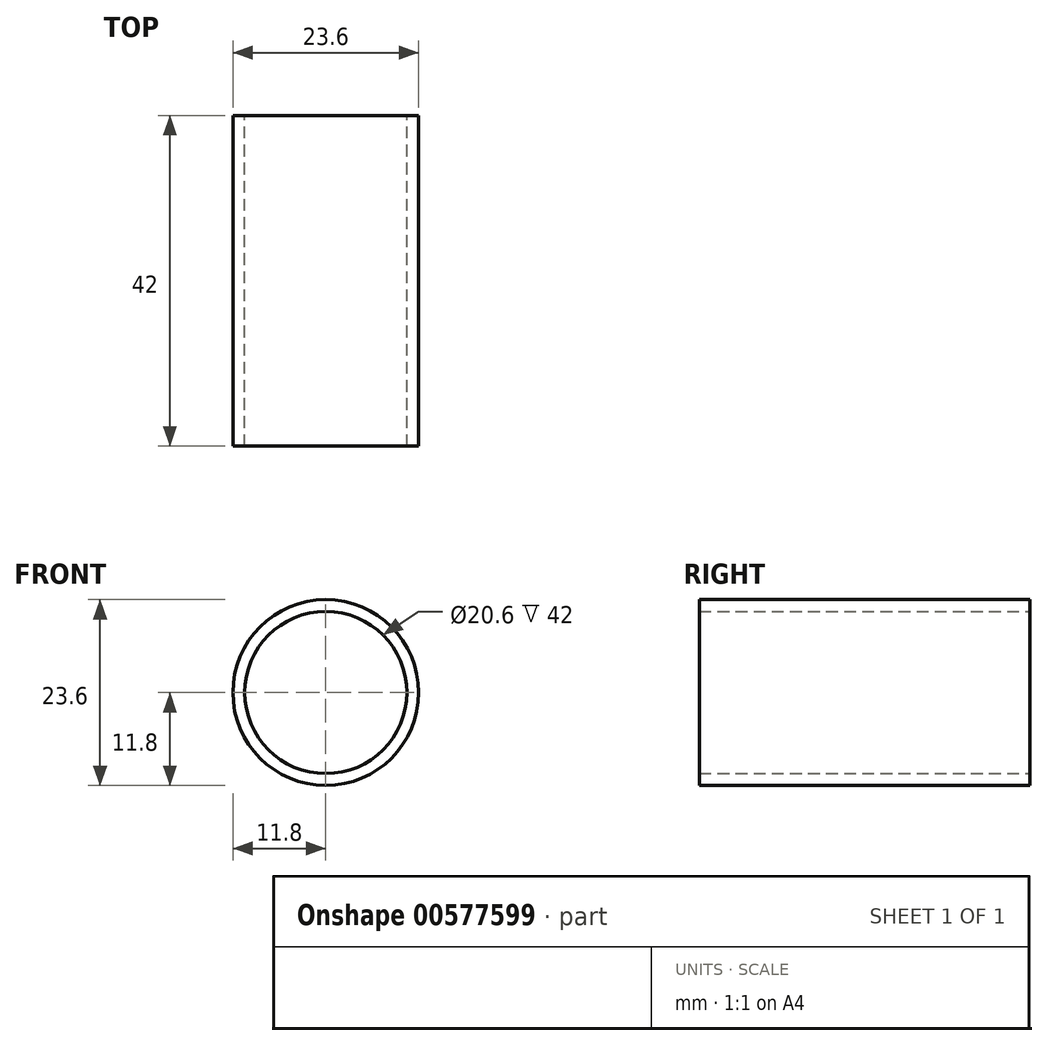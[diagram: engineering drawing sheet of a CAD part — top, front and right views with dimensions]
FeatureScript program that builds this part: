
annotation { "Feature Type Name" : "Feature", "Feature Type Description" : "" }
export const myFeature = defineFeature(function(context is Context, id is Id, definition is map)
    precondition{}
    {
        {
            var Q0;
            Q0=qCreatedBy(makeId("Front.planeOp"),FACE);
            var sketch = newSketch(context, id + "F0", { "sketchPlane" : qUnion([Q0])});
            skCircle(sketch, "E0", {"center": v(0, 0) * mm, "radius": 11.8 * mm});
            skCircle(sketch, "E1", {"center": v(0, 0) * mm, "radius": 10.3 * mm});
            skSolve(sketch);
        }
        {
            var Q0;
            Q0 = qSketchRegion(id + "F0", true);
            extrude(context, id + "F1", {"entities" : qUnion([Q0]), "depth" : 42 * mm, "offsetDistance" : 25.4 * mm});
        }
    });
